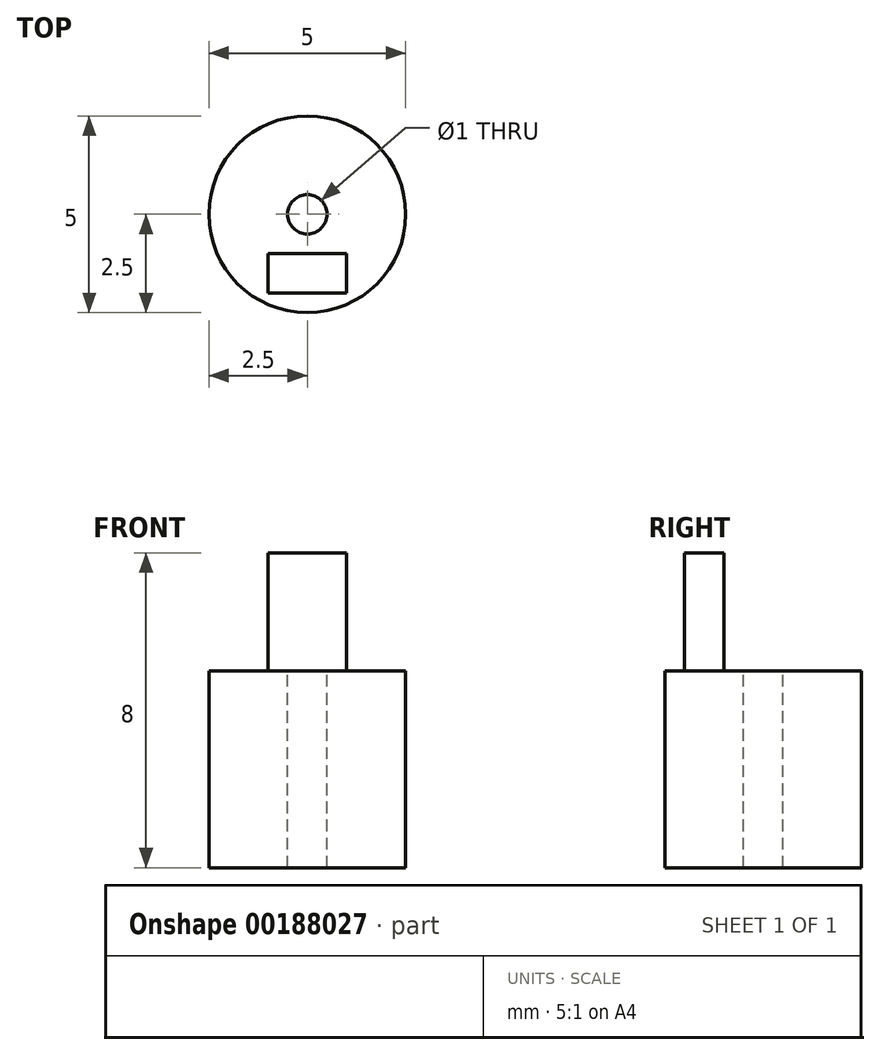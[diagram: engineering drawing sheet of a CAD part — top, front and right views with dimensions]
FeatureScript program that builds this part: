
annotation { "Feature Type Name" : "Feature", "Feature Type Description" : "" }
export const myFeature = defineFeature(function(context is Context, id is Id, definition is map)
    precondition{}
    {
        {
            var Q0;
            Q0=qCreatedBy(makeId("Top.planeOp"),FACE);
            var sketch = newSketch(context, id + "F0", { "sketchPlane" : qUnion([Q0])});
            skCircle(sketch, "E0", {"center": v(0, 0) * mm, "radius": 2.5 * mm});
            skSolve(sketch);
        }
        {
            var Q0;
            Q0=qSketchRegion(id+"F0",true);
            extrude(context, id + "F1", {"entities" : qUnion([Q0]), "depth" : 5 * mm});
        }
        {
            var Q0;
            Q0=makeQuery(id+"F1.opExtrude","CAP_FACE",FACE,{"disambiguationData":[OSD([sQuery(id+"F0.wireOp",EDGE,"E0")])],"isStart":false});
            var sketch = newSketch(context, id + "F2", { "sketchPlane" : qUnion([Q0])});
            skLineSegment(sketch, "E1.bottom", {"start": v(-1, -1) * mm, "end": v(1, -1) * mm});
            skLineSegment(sketch, "E1.top", {"start": v(-1, -2) * mm, "end": v(1, -2) * mm});
            skLineSegment(sketch, "E1.left", {"start": v(-1, -1) * mm, "end": v(-1, -2) * mm});
            skLineSegment(sketch, "E1.right", {"start": v(1, -1) * mm, "end": v(1, -2) * mm});
            skSolve(sketch);
        }
        {
            var Q0;
            Q0=qSketchRegion(id+"F2",true);
            extrude(context, id + "F3", {"entities" : qUnion([Q0]), "operationType" : NewBodyOperationType.ADD, "depth" : 3 * mm});
        }
        {
            var Q0;
            Q0=makeQuery(id+"F1.opExtrude","CAP_FACE",FACE,{"disambiguationData":[OSD([sQuery(id+"F0.wireOp",EDGE,"E0")])],"isStart":false});
            var sketch = newSketch(context, id + "F4", { "sketchPlane" : qUnion([Q0])});
            skCircle(sketch, "E2", {"center": v(0, 0) * mm, "radius": 0.5 * mm});
            skSolve(sketch);
        }
        {
            var Q0;
            Q0 = qSketchRegion(id + "F4", true);
            extrude(context, id + "F5", {"entities" : qUnion([Q0]), "operationType" : NewBodyOperationType.REMOVE, "oppositeDirection" : true, "depth" : 25 * mm});
        }
    });
